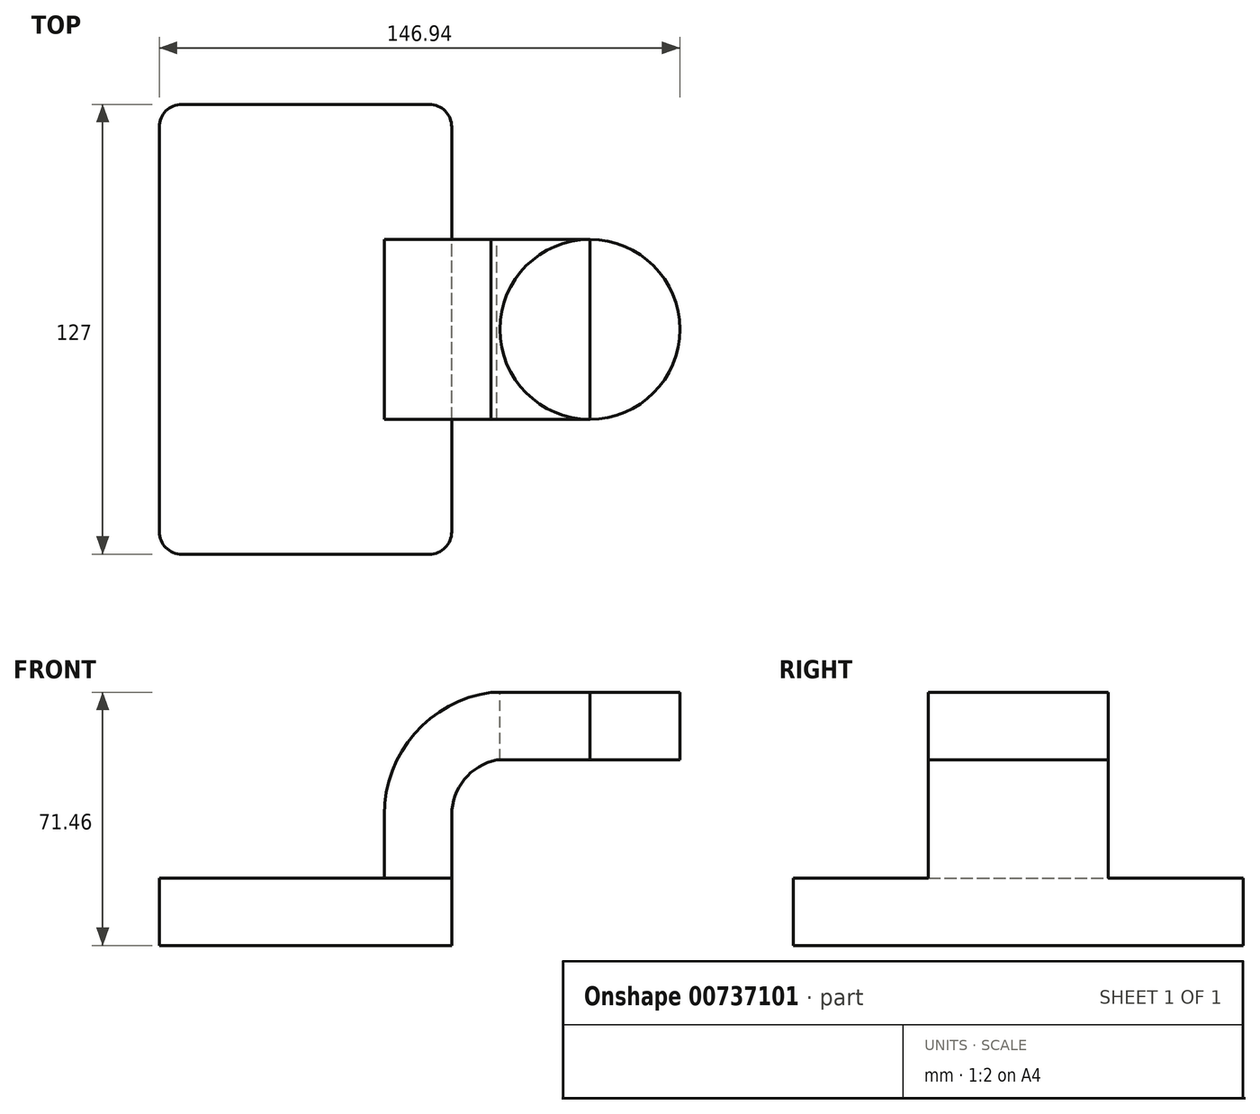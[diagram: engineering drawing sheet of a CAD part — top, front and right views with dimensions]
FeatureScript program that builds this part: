
annotation { "Feature Type Name" : "Feature", "Feature Type Description" : "" }
export const myFeature = defineFeature(function(context is Context, id is Id, definition is map)
    precondition{}
    {
        {
            var Q0;
            Q0=qCreatedBy(makeId("Front.planeOp"),FACE);
            var sketch = newSketch(context, id + "F0", { "sketchPlane" : qUnion([Q0])});
            skLineSegment(sketch, "E0.bottom", {"start": v(41.27, 9.53) * mm, "end": v(-41.28, 9.53) * mm});
            skLineSegment(sketch, "E0.top", {"start": v(41.28, -9.52) * mm, "end": v(-41.27, -9.52) * mm});
            skLineSegment(sketch, "E0.left", {"start": v(41.27, 9.53) * mm, "end": v(41.28, -9.52) * mm});
            skLineSegment(sketch, "E0.right", {"start": v(-41.28, 9.53) * mm, "end": v(-41.27, -9.52) * mm});
            skPoint(sketch, "E0.middle", {"position": v(0, 0) * mm});
            skLineSegment(sketch, "E1.bottom", {"start": v(131.07, 66.68) * mm, "end": v(80.27, 66.68) * mm});
            skLineSegment(sketch, "E1.top", {"start": v(131.07, 38.1) * mm, "end": v(80.27, 38.1) * mm});
            skLineSegment(sketch, "E1.left", {"start": v(131.07, 66.68) * mm, "end": v(131.07, 38.1) * mm});
            skLineSegment(sketch, "E1.right", {"start": v(80.27, 66.68) * mm, "end": v(80.27, 38.1) * mm});
            skPoint(sketch, "E1.middle", {"position": v(105.67, 52.39) * mm});
            skLineSegment(sketch, "E2", {"start": v(41.27, 9.53) * mm, "end": v(41.27, 27.32) * mm});
            skArc(sketch, "E3", {"start": v(41.27, 27.32) * mm, "mid": v(44.85, 37.36) * mm, "end": v(53.97, 42.88) * mm});
            skLineSegment(sketch, "E4", {"start": v(53.97, 42.88) * mm, "end": v(85.73, 42.88) * mm});
            skLineSegment(sketch, "E5.0", {"start": v(52.42, 61.93) * mm, "end": v(85.73, 61.93) * mm});
            skArc(sketch, "E5.1", {"start": v(22.22, 27.32) * mm, "mid": v(30.84, 50.28) * mm, "end": v(52.42, 61.93) * mm});
            skLineSegment(sketch, "E5.2", {"start": v(22.22, 9.53) * mm, "end": v(22.22, 27.32) * mm});
            skLineSegment(sketch, "E6", {"start": v(85.73, 66.68) * mm, "end": v(85.73, 38.1) * mm});
            skFitSpline(sketch, "E7", {"points": [v(-41.28, 9.53) * mm, v(52.42, 61.93) * mm], "startDerivative": vector(-1.65, 92.3) * mm, "endDerivative": vector(127.17, 3.43) * mm});
            skSolve(sketch);
        }
        {
            var Q0;
            Q0=makeQuery(id+"F0.imprint","IMPRINT",FACE,{"disambiguationData":[TD([[makeQuery(id+"F0.imprint","IMPRINT",EDGE,{"derivedFrom":sQuery(id+"F0.wireOp",EDGE,"E0.top")}),-1.0]])]});
            extrude(context, id + "F1", {"entities" : qUnion([Q0]), "endBound" : BoundingType.SYMMETRIC, "depth" : 127 * mm, "offsetDistance" : 25.4 * mm});
        }
        {
            var Q0;
            {var subQ1=sQuery(id+"F0.wireOp",EDGE,"E2");Q0=makeQuery(id+"F0.imprint","IMPRINT",FACE,{"disambiguationData":[TD([[makeQuery(id+"F0.imprint","IMPRINT",EDGE,{"derivedFrom":subQ1}),1.0]])]});}
            extrude(context, id + "F2", {"entities" : qUnion([Q0]), "operationType" : NewBodyOperationType.ADD, "endBound" : BoundingType.SYMMETRIC, "depth" : 50.8 * mm, "offsetDistance" : 25.4 * mm});
        }
        {
            var Q0;
            Q0=makeQuery(id+"F0.imprint","IMPRINT",FACE,{"disambiguationData":[TD([[makeQuery(id+"F0.imprint","IMPRINT",EDGE,{"derivedFrom":sQuery(id+"F0.wireOp",EDGE,"E5.1")}),1.0]])]});
            extrude(context, id + "F3", {"entities" : qUnion([Q0]), "operationType" : NewBodyOperationType.ADD, "endBound" : BoundingType.SYMMETRIC, "depth" : 15.88 * mm, "offsetDistance" : 25.4 * mm});
        }
        {
            var Q0;
            Q0=makeQuery(id+"F2.opExtrude","SWEPT_FACE",FACE,{"disambiguationData":[OSD([sQuery(id+"F0.wireOp",EDGE,"E1.right")])]});
            var sketch = newSketch(context, id + "F4", { "sketchPlane" : qUnion([Q0])});
            skLineSegment(sketch, "E8", {"start": v(0, 61.93) * mm, "end": v(0, 42.88) * mm});
            skSolve(sketch);
        }
        {
            var Q0;
            {var subQ0=sQuery(id+"F4.wireOp",EDGE,"E8");Q0=makeQuery(id+"F4.imprint","IMPRINT",FACE,{"disambiguationData":[TD([[makeQuery(id+"F4.imprint","IMPRINT",EDGE,{"derivedFrom":subQ0}),-1.0]])]});}
            var Q1;
            Q1=sQuery(id+"F4.wireOp",EDGE,"E8");
            revolve(context, id + "F5", {"surfaceOperationType" : NewSurfaceOperationType.NEW, "entities" : qUnion([Q0]), "axis" : qUnion([Q1]), "revolveType" : RevolveType.FULL});
        }
        {
            var Q0;
            Q0=makeQuery(id+"F1.opExtrude","CAP_EDGE",EDGE,{"disambiguationData":[OSD([sQuery(id+"F0.wireOp",EDGE,"E0.left")])],"isStart":false});
            var Q1;
            Q1=makeQuery(id+"F1.opExtrude","CAP_EDGE",EDGE,{"disambiguationData":[OSD([sQuery(id+"F0.wireOp",EDGE,"E0.left")])],"isStart":true});
            var Q2;
            Q2=makeQuery(id+"F1.opExtrude","CAP_EDGE",EDGE,{"disambiguationData":[OSD([sQuery(id+"F0.wireOp",EDGE,"E0.right")])],"isStart":true});
            var Q3;
            Q3=makeQuery(id+"F1.opExtrude","CAP_EDGE",EDGE,{"disambiguationData":[OSD([sQuery(id+"F0.wireOp",EDGE,"E0.right")])],"isStart":false});
            fillet(context, id + "F6", {"entities" : qUnion([Q0, Q1, Q2, Q3]), "radius" : 6.35 * mm, "tangentPropagation" : true, "allowEdgeOverflow" : false});
        }
    });
